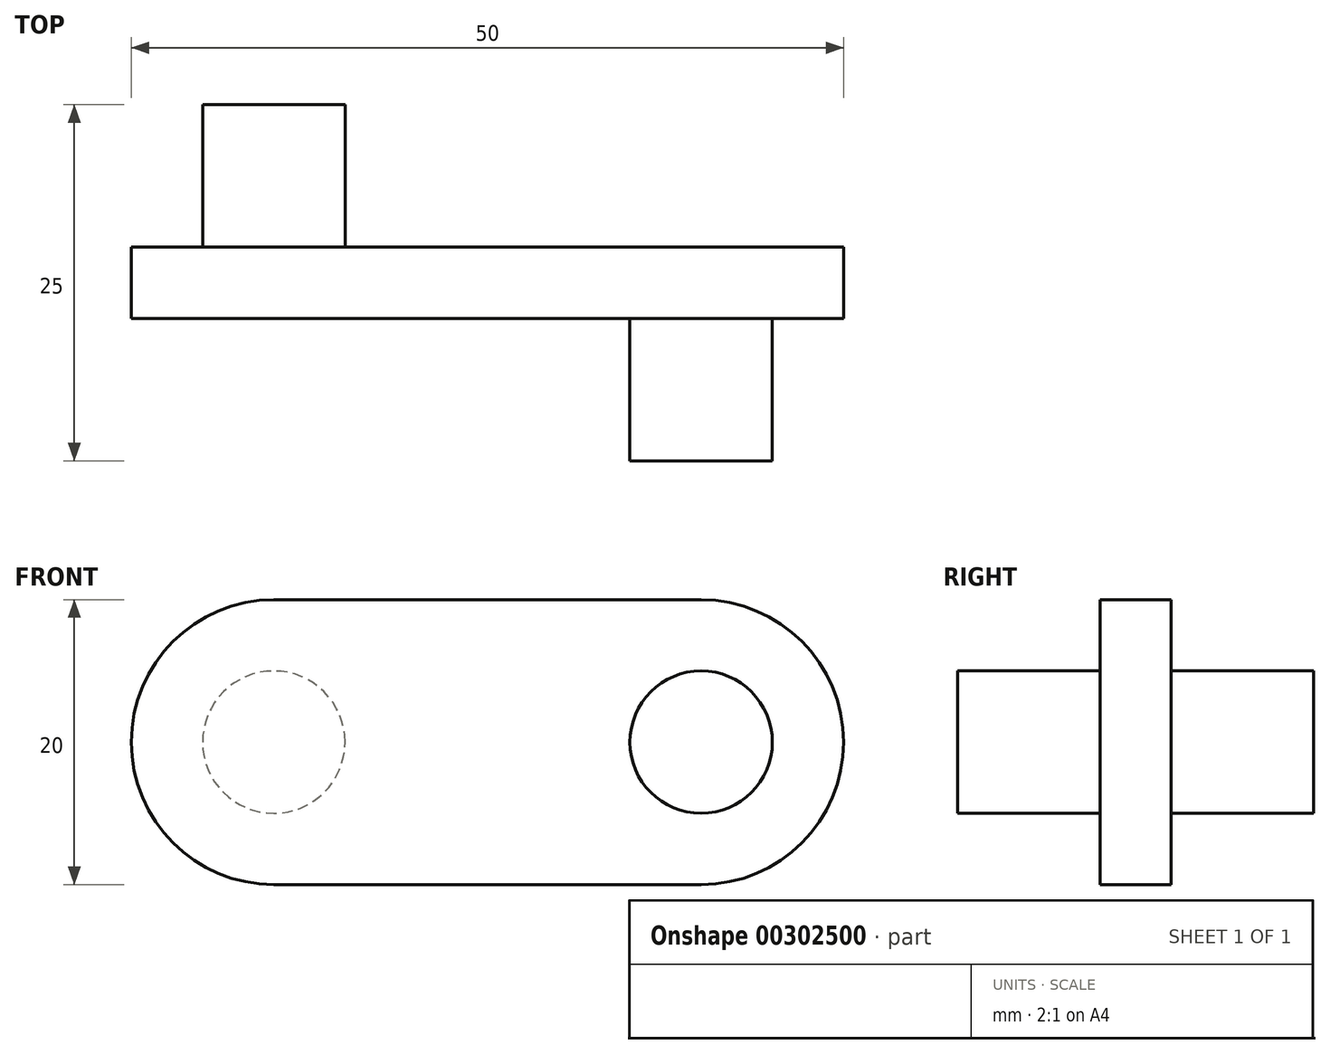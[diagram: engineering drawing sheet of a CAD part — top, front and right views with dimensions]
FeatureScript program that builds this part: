
annotation { "Feature Type Name" : "Feature", "Feature Type Description" : "" }
export const myFeature = defineFeature(function(context is Context, id is Id, definition is map)
    precondition{}
    {
        {
            var Q0;
            Q0=qCreatedBy(makeId("Front.planeOp"),FACE);
            var sketch = newSketch(context, id + "F0", { "sketchPlane" : qUnion([Q0])});
            skLineSegment(sketch, "E0", {"start": v(-15, 0) * mm, "end": v(15, 0) * mm, "construction": true});
            skArc(sketch, "E1.0.startCap", {"start": v(-15, -10) * mm, "mid": v(-25, 0) * mm, "end": v(-15, 10) * mm});
            skArc(sketch, "E1.0.endCap", {"start": v(15, 10) * mm, "mid": v(25, 0) * mm, "end": v(15, -10) * mm});
            skLineSegment(sketch, "E1.0.left", {"start": v(-15, 10) * mm, "end": v(15, 10) * mm});
            skLineSegment(sketch, "E1.0.right", {"start": v(-15, -10) * mm, "end": v(15, -10) * mm});
            skSolve(sketch);
        }
        {
            var Q0;
            Q0 = qSketchRegion(id + "F0", true);
            extrude(context, id + "F1", {"entities" : qUnion([Q0]), "depth" : 5 * mm});
        }
        {
            var Q0;
            Q0=makeQuery(id+"F1.opExtrude","CAP_FACE",FACE,{"disambiguationData":[OSD([sQuery(id+"F0.wireOp",EDGE,"E1.0.startCap"),sQuery(id+"F0.wireOp",EDGE,"E1.0.endCap"),sQuery(id+"F0.wireOp",EDGE,"E1.0.left"),sQuery(id+"F0.wireOp",EDGE,"E1.0.right")])],"isStart":false});
            var sketch = newSketch(context, id + "F2", { "sketchPlane" : qUnion([Q0])});
            skCircle(sketch, "E2", {"center": v(15, 0) * mm, "radius": 5 * mm});
            skSolve(sketch);
        }
        {
            var Q0;
            Q0 = qSketchRegion(id + "F2", true);
            extrude(context, id + "F3", {"entities" : qUnion([Q0]), "operationType" : NewBodyOperationType.ADD, "depth" : 10 * mm});
        }
        {
            var Q0;
            Q0=makeQuery(id+"F1.opExtrude","CAP_FACE",FACE,{"disambiguationData":[OSD([sQuery(id+"F0.wireOp",EDGE,"E1.0.startCap"),sQuery(id+"F0.wireOp",EDGE,"E1.0.endCap"),sQuery(id+"F0.wireOp",EDGE,"E1.0.left"),sQuery(id+"F0.wireOp",EDGE,"E1.0.right")])],"isStart":true});
            var sketch = newSketch(context, id + "F4", { "sketchPlane" : qUnion([Q0])});
            skCircle(sketch, "E3", {"center": v(15, 0) * mm, "radius": 5 * mm});
            skSolve(sketch);
        }
        {
            var Q0;
            Q0 = qSketchRegion(id + "F4", true);
            extrude(context, id + "F5", {"entities" : qUnion([Q0]), "operationType" : NewBodyOperationType.ADD, "depth" : 10 * mm});
        }
    });
